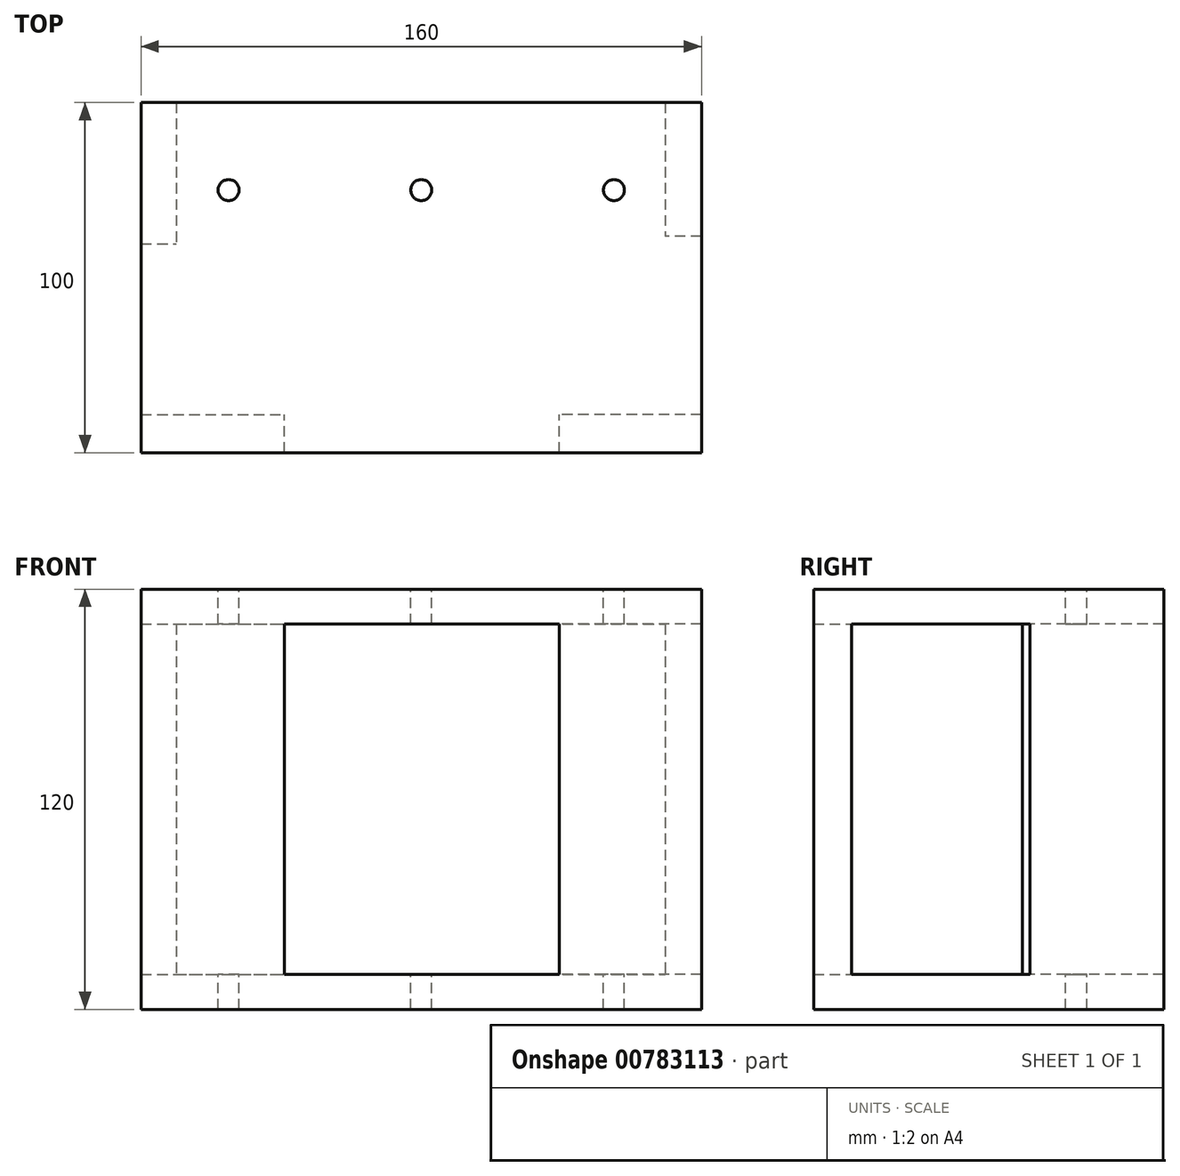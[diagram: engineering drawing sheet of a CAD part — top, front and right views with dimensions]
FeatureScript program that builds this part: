
annotation { "Feature Type Name" : "Feature", "Feature Type Description" : "" }
export const myFeature = defineFeature(function(context is Context, id is Id, definition is map)
    precondition{}
    {
        {
            var Q0;
            Q0=qCreatedBy(makeId("Top.planeOp"),FACE);
            var sketch = newSketch(context, id + "F0", { "sketchPlane" : qUnion([Q0])});
            skLineSegment(sketch, "E0.bottom", {"start": v(-55.62, -63.53) * mm, "end": v(104.38, -63.53) * mm});
            skLineSegment(sketch, "E0.top", {"start": v(-55.62, 36.47) * mm, "end": v(104.38, 36.47) * mm});
            skLineSegment(sketch, "E0.left", {"start": v(-55.62, -63.53) * mm, "end": v(-55.62, 36.47) * mm});
            skLineSegment(sketch, "E0.right", {"start": v(104.38, -63.53) * mm, "end": v(104.38, 36.47) * mm});
            skSolve(sketch);
        }
        {
            var Q0;
            Q0=qSketchRegion(id+"F0",true);
            var Q1;
            Q1=makeQuery(id+"F0.imprint","IMPRINT",FACE,{"disambiguationData":[TD([[makeQuery(id+"F0.imprint","IMPRINT",EDGE,{"derivedFrom":sQuery(id+"F0.wireOp",EDGE,"E0.bottom")}),1.0]])]});
            extrude(context, id + "F1", {"entities" : qUnion([Q0, Q1]), "depth" : 10 * mm});
        }
        {
            var Q0;
            Q0=makeQuery(id+"F1.opExtrude","CAP_FACE",FACE,{"disambiguationData":[OSD([sQuery(id+"F0.wireOp",EDGE,"E0.bottom"),sQuery(id+"F0.wireOp",EDGE,"E0.top"),sQuery(id+"F0.wireOp",EDGE,"E0.left"),sQuery(id+"F0.wireOp",EDGE,"E0.right")])],"isStart":false});
            var sketch = newSketch(context, id + "F2", { "sketchPlane" : qUnion([Q0])});
            skLineSegment(sketch, "E1.bottom", {"start": v(-55.62, -63.53) * mm, "end": v(-14.72, -63.53) * mm});
            skLineSegment(sketch, "E1.top", {"start": v(-55.62, -52.68) * mm, "end": v(-14.72, -52.68) * mm});
            skLineSegment(sketch, "E1.left", {"start": v(-55.62, -63.53) * mm, "end": v(-55.62, -52.68) * mm});
            skLineSegment(sketch, "E1.right", {"start": v(-14.72, -63.53) * mm, "end": v(-14.72, -52.68) * mm});
            skSolve(sketch);
        }
        {
            var Q0;
            Q0=qSketchRegion(id+"F2",true);
            extrude(context, id + "F3", {"entities" : qUnion([Q0]), "operationType" : NewBodyOperationType.ADD, "depth" : 100 * mm});
        }
        {
            var Q0;
            Q0=makeQuery(id+"F1.opExtrude","CAP_FACE",FACE,{"disambiguationData":[OSD([sQuery(id+"F0.wireOp",EDGE,"E0.bottom"),sQuery(id+"F0.wireOp",EDGE,"E0.top"),sQuery(id+"F0.wireOp",EDGE,"E0.left"),sQuery(id+"F0.wireOp",EDGE,"E0.right")])],"isStart":false});
            var sketch = newSketch(context, id + "F4", { "sketchPlane" : qUnion([Q0])});
            skLineSegment(sketch, "E2.bottom", {"start": v(104.38, -63.53) * mm, "end": v(63.77, -63.53) * mm});
            skLineSegment(sketch, "E2.top", {"start": v(104.38, -52.65) * mm, "end": v(63.77, -52.65) * mm});
            skLineSegment(sketch, "E2.left", {"start": v(104.38, -63.53) * mm, "end": v(104.38, -52.65) * mm});
            skLineSegment(sketch, "E2.right", {"start": v(63.77, -63.53) * mm, "end": v(63.77, -52.65) * mm});
            skSolve(sketch);
        }
        {
            var Q0;
            Q0=qSketchRegion(id+"F4",true);
            extrude(context, id + "F5", {"entities" : qUnion([Q0]), "operationType" : NewBodyOperationType.ADD, "depth" : 100 * mm});
        }
        {
            var Q0;
            Q0=makeQuery(id+"F1.opExtrude","CAP_FACE",FACE,{"disambiguationData":[OSD([sQuery(id+"F0.wireOp",EDGE,"E0.bottom"),sQuery(id+"F0.wireOp",EDGE,"E0.top"),sQuery(id+"F0.wireOp",EDGE,"E0.left"),sQuery(id+"F0.wireOp",EDGE,"E0.right")])],"isStart":false});
            var sketch = newSketch(context, id + "F6", { "sketchPlane" : qUnion([Q0])});
            skLineSegment(sketch, "E3.bottom", {"start": v(104.38, 36.47) * mm, "end": v(94.06, 36.47) * mm});
            skLineSegment(sketch, "E3.top", {"start": v(104.38, -1.74) * mm, "end": v(94.06, -1.74) * mm});
            skLineSegment(sketch, "E3.left", {"start": v(104.38, 36.47) * mm, "end": v(104.38, -1.74) * mm});
            skLineSegment(sketch, "E3.right", {"start": v(94.06, 36.47) * mm, "end": v(94.06, -1.74) * mm});
            skSolve(sketch);
        }
        {
            var Q0;
            Q0=qSketchRegion(id+"F6",true);
            extrude(context, id + "F7", {"entities" : qUnion([Q0]), "operationType" : NewBodyOperationType.ADD, "depth" : 100 * mm});
        }
        {
            var Q0;
            Q0=makeQuery(id+"F1.opExtrude","CAP_FACE",FACE,{"disambiguationData":[OSD([sQuery(id+"F0.wireOp",EDGE,"E0.bottom"),sQuery(id+"F0.wireOp",EDGE,"E0.top"),sQuery(id+"F0.wireOp",EDGE,"E0.left"),sQuery(id+"F0.wireOp",EDGE,"E0.right")])],"isStart":false});
            var sketch = newSketch(context, id + "F8", { "sketchPlane" : qUnion([Q0])});
            skLineSegment(sketch, "E4.bottom", {"start": v(-55.62, 36.47) * mm, "end": v(-45.61, 36.47) * mm});
            skLineSegment(sketch, "E4.top", {"start": v(-55.62, -3.9) * mm, "end": v(-45.61, -3.9) * mm});
            skLineSegment(sketch, "E4.left", {"start": v(-55.62, 36.47) * mm, "end": v(-55.62, -3.9) * mm});
            skLineSegment(sketch, "E4.right", {"start": v(-45.61, 36.47) * mm, "end": v(-45.61, -3.9) * mm});
            skSolve(sketch);
        }
        {
            var Q0;
            Q0=qSketchRegion(id+"F8",true);
            extrude(context, id + "F9", {"entities" : qUnion([Q0]), "operationType" : NewBodyOperationType.ADD, "depth" : 100 * mm});
        }
        {
            var Q0;
            Q0=makeQuery(id+"F3.opExtrude","CAP_FACE",FACE,{"disambiguationData":[OSD([sQuery(id+"F2.wireOp",EDGE,"E1.bottom"),sQuery(id+"F2.wireOp",EDGE,"E1.top"),sQuery(id+"F2.wireOp",EDGE,"E1.left"),sQuery(id+"F2.wireOp",EDGE,"E1.right")])],"isStart":false});
            var sketch = newSketch(context, id + "F10", { "sketchPlane" : qUnion([Q0])});
            skLineSegment(sketch, "E5.bottom", {"start": v(-55.62, -63.53) * mm, "end": v(104.38, -63.53) * mm});
            skLineSegment(sketch, "E5.top", {"start": v(-55.62, 36.47) * mm, "end": v(104.38, 36.47) * mm});
            skLineSegment(sketch, "E5.left", {"start": v(-55.62, -63.53) * mm, "end": v(-55.62, 36.47) * mm});
            skLineSegment(sketch, "E5.right", {"start": v(104.38, -63.53) * mm, "end": v(104.38, 36.47) * mm});
            skSolve(sketch);
        }
        {
            var Q0;
            Q0=qSketchRegion(id+"F10",true);
            extrude(context, id + "F11", {"entities" : qUnion([Q0]), "operationType" : NewBodyOperationType.ADD, "depth" : 10 * mm});
        }
        {
            var Q0;
            Q0=makeQuery(id+"F11.opExtrude","CAP_FACE",FACE,{"disambiguationData":[OSD([sQuery(id+"F10.wireOp",EDGE,"E5.bottom"),sQuery(id+"F10.wireOp",EDGE,"E5.top"),sQuery(id+"F10.wireOp",EDGE,"E5.left"),sQuery(id+"F10.wireOp",EDGE,"E5.right")])],"isStart":false});
            var sketch = newSketch(context, id + "F12", { "sketchPlane" : qUnion([Q0])});
            skCircle(sketch, "E6", {"center": v(79.38, 11.47) * mm, "radius": 2.39 * mm});
            skCircle(sketch, "E7", {"center": v(24.38, 11.47) * mm, "radius": 1.5 * mm});
            skCircle(sketch, "E8", {"center": v(-30.62, 11.47) * mm, "radius": 1.92 * mm});
            skSolve(sketch);
        }
        {
            var Q0;
            Q0=sQuery(id+"F12.wireOp",VERTEX,"E6.center");
            var Q1;
            Q1=sQuery(id+"F12.wireOp",VERTEX,"E7.center");
            var Q2;
            Q2=sQuery(id+"F12.wireOp",VERTEX,"E8.center");
            var Q3;
            Q3=makeQuery(id+"F1.opExtrude","SWEPT_BODY",BODY,{"disambiguationData":[OSD([sQuery(id+"F0.wireOp",EDGE,"E0.bottom"),sQuery(id+"F0.wireOp",EDGE,"E0.top"),sQuery(id+"F0.wireOp",EDGE,"E0.left"),sQuery(id+"F0.wireOp",EDGE,"E0.right")])]});
            hole(context, id + "F13", {"style" : HoleStyle.SIMPLE, "endStyle" : HoleEndStyle.THROUGH, "holeDiameter" : 6 * mm, "majorDiameter" : 5 * mm, "isTappedThrough" : true, "tappedDepth" : 12 * mm, "tapClearance" : 3, "locations" : qUnion([Q0, Q1, Q2]), "scope" : qUnion([Q3])});
        }
    });
